# Revit family: Electrical_Switchgear_Modelec_M-collection-single_FRA888
name_source: partatom
category: Installations électriques
units: mm (PartAtom-declared; Revit-internal decimal feet)

## family parameters
Conserver l'orientation des annotations = Non
Cote de connecteur circulaire = Utiliser le diamètre
Couper avec des vides une fois chargée = Non
Hôte = Face
Numéro OmniClass = 23.80.50.11.14
Partagée = Non
Repere pour localisation dans la piece = Non
Titre OmniClass = Switches
Type d'élément = Normal

## types (1)
- Par défaut - veuillez charger le catalogue des types de familles Revit
    Apparent Load = 0 VA
    B1 = Oui
    B2 = Non
    C1 = Non
    C1 et C3 = Non
    C3 = Non
    Couleur du Mécanisme = Modelec - Metal - Noir Mat
    Description = Conçue par Valérie Mazerat, la collection M de commutateurs et de prises a émergé du matériau lui-même. Produit d'un mariage entre le style des années 60 et notre propre savoir-faire contemporain, elle a une touche de temps passé, résonnant dans le présent. La collection M s'intègre parfaitement dans des environnements contemporains, minimalistes et épurés, des lieux qui apprécient la simplicité.
    Description du connecteur = Interrupteur
    Détecteur Mouv = Non
    Elévation par défaut = 0 mm  [stored 0 ft]
    Fabricant = Modelec
    Installation instructions = https://www.modelec.com
    Interrupteur à Carte = Non
    K1 = Non
    M1 = Non
    M2 = Non
    Modèle = M Collection
    Number of Poles = 1
    O1 = Non
    O1, R2, SC = Non
    Power Factor = 1
    Product Documentation Link = https://www.modelec.com
    Product Page URL = https://www.modelec.com
    Product data url = https://bimobject.com
    Quantité 1 = 3
    Quantité 2 = 3
    R1 = Non
    R2 = Non
    SC = Non
    U1 = Non
    URL = https://www.modelec.com
    V1 = Non
    Version = 1
    Voltage = 220 V
    Weight - Mass = 0.12 kg

note: [stored X ft] marks values corroborated as IEEE doubles in the binary element streams (Revit-internal decimal feet)

## geometry (parser evidence)
native form markers: Sweep x2
no freeform markers — native parametric forms only
